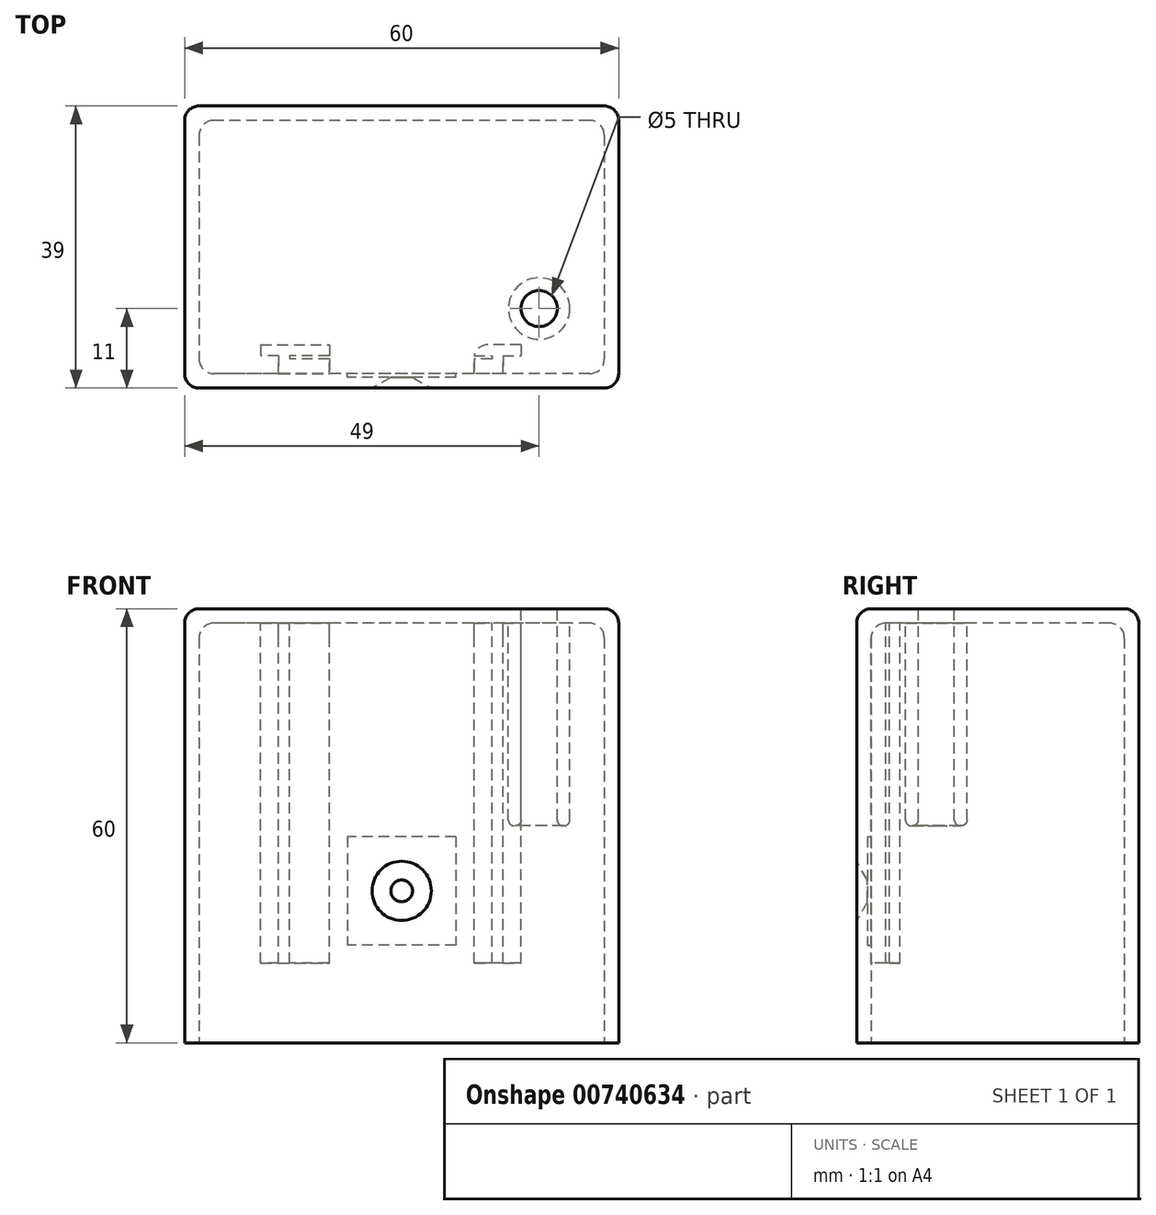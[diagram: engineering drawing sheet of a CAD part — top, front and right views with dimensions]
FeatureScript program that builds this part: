
annotation { "Feature Type Name" : "Feature", "Feature Type Description" : "" }
export const myFeature = defineFeature(function(context is Context, id is Id, definition is map)
    precondition{}
    {
        {
            var Q0;
            Q0=qCreatedBy(makeId("Top.planeOp"),FACE);
            var sketch = newSketch(context, id + "F0", { "sketchPlane" : qUnion([Q0])});
            skLineSegment(sketch, "E0.bottom", {"start": v(30, 19.5) * mm, "end": v(-30, 19.5) * mm});
            skLineSegment(sketch, "E0.top", {"start": v(30, -19.5) * mm, "end": v(-30, -19.5) * mm});
            skLineSegment(sketch, "E0.left", {"start": v(30, 19.5) * mm, "end": v(30, -19.5) * mm});
            skLineSegment(sketch, "E0.right", {"start": v(-30, 19.5) * mm, "end": v(-30, -19.5) * mm});
            skPoint(sketch, "E0.middle", {"position": v(0, 0) * mm});
            skSolve(sketch);
        }
        {
            var Q0;
            Q0 = qSketchRegion(id + "F0", true);
            extrude(context, id + "F1", {"entities" : qUnion([Q0]), "depth" : 60 * mm, "offsetDistance" : 25 * mm});
        }
        {
            var Q0;
            Q0=makeQuery(id+"F1.opExtrude","CAP_FACE",FACE,{"disambiguationData":[OSD([sQuery(id+"F0.wireOp",EDGE,"E0.bottom"),sQuery(id+"F0.wireOp",EDGE,"E0.top"),sQuery(id+"F0.wireOp",EDGE,"E0.left"),sQuery(id+"F0.wireOp",EDGE,"E0.right")])],"isStart":true});
            shell(context, id + "F2", {"entities" : qUnion([Q0]), "thickness" : 2 * mm});
        }
        {
            var Q0;
            Q0=makeQuery(id+"F1.opExtrude","SWEPT_EDGE",EDGE,{"disambiguationData":[OSD([sQuery(id+"F0.wireOp",EDGE,"E0.bottom"),sQuery(id+"F0.wireOp",EDGE,"E0.left")])]});
            var Q1;
            Q1=makeQuery(id+"F1.opExtrude","CAP_EDGE",EDGE,{"disambiguationData":[OSD([sQuery(id+"F0.wireOp",EDGE,"E0.bottom")])],"isStart":false});
            var Q2;
            Q2=makeQuery(id+"F1.opExtrude","SWEPT_EDGE",EDGE,{"disambiguationData":[OSD([sQuery(id+"F0.wireOp",EDGE,"E0.bottom"),sQuery(id+"F0.wireOp",EDGE,"E0.right")])]});
            var Q3;
            Q3=makeQuery(id+"F1.opExtrude","SWEPT_EDGE",EDGE,{"disambiguationData":[OSD([sQuery(id+"F0.wireOp",EDGE,"E0.top"),sQuery(id+"F0.wireOp",EDGE,"E0.right")])]});
            var Q4;
            Q4=makeQuery(id+"F1.opExtrude","CAP_EDGE",EDGE,{"disambiguationData":[OSD([sQuery(id+"F0.wireOp",EDGE,"E0.right")])],"isStart":false});
            var Q5;
            Q5=makeQuery(id+"F1.opExtrude","CAP_EDGE",EDGE,{"disambiguationData":[OSD([sQuery(id+"F0.wireOp",EDGE,"E0.top")])],"isStart":false});
            var Q6;
            Q6=makeQuery(id+"F1.opExtrude","SWEPT_EDGE",EDGE,{"disambiguationData":[OSD([sQuery(id+"F0.wireOp",EDGE,"E0.top"),sQuery(id+"F0.wireOp",EDGE,"E0.left")])]});
            var Q7;
            Q7=makeQuery(id+"F1.opExtrude","CAP_EDGE",EDGE,{"disambiguationData":[OSD([sQuery(id+"F0.wireOp",EDGE,"E0.left")])],"isStart":false});
            var Q8;
            Q8=makeQuery(id+"F2.opShell","OFFSET_EDGE",EDGE,{"disambiguationData":[OSD([sQuery(id+"F0.wireOp",EDGE,"E0.top"),sQuery(id+"F0.wireOp",EDGE,"E0.right")])]});
            var Q9;
            Q9=makeQuery(id+"F2.opShell","OFFSET_EDGE",EDGE,{"disambiguationData":[OSD([sQuery(id+"F0.wireOp",EDGE,"E0.top"),sQuery(id+"F0.wireOp",EDGE,"E0.left")])]});
            var Q10;
            {var subQ0=sQuery(id+"F0.wireOp",EDGE,"E0.bottom");var subQ1=sQuery(id+"F0.wireOp",EDGE,"E0.left");Q10=makeQuery(id+"F9EDMC7BK73mlxk_1.boolean.opBoolean","SPLIT",EDGE,{"disambiguationData":[topologyDisambiguationEdgeConnected([makeQuery(id+"F2.opShell","OFFSET_FACE",FACE,{"disambiguationData":[OSD([subQ0])]})])],"derivedFrom":makeQuery(id+"F2.opShell","OFFSET_EDGE",EDGE,{"disambiguationData":[OSD([subQ0,subQ1])]})});}
            var Q11;
            Q11=makeQuery(id+"F2.opShell","OFFSET_EDGE",EDGE,{"disambiguationData":[OSD([sQuery(id+"F0.wireOp",EDGE,"E0.bottom"),sQuery(id+"F0.wireOp",EDGE,"E0.right")])]});
            var Q12;
            {var subQ0=sQuery(id+"F0.wireOp",EDGE,"E0.bottom");Q12=makeQuery(id+"F2.opShell","OFFSET_EDGE",EDGE,{"disambiguationData":[OSD([subQ0]),TDD([makeQuery(id+"F1.opExtrude","CAP_EDGE",EDGE,{"disambiguationData":[OSD([subQ0])],"isStart":false})])]});}
            var Q13;
            {var subQ0=sQuery(id+"F0.wireOp",EDGE,"E0.right");Q13=makeQuery(id+"F2.opShell","OFFSET_EDGE",EDGE,{"disambiguationData":[OSD([subQ0]),TDD([makeQuery(id+"F1.opExtrude","CAP_EDGE",EDGE,{"disambiguationData":[OSD([subQ0])],"isStart":false})])]});}
            var Q14;
            {var subQ0=sQuery(id+"F0.wireOp",EDGE,"E0.left");Q14=makeQuery(id+"F2.opShell","OFFSET_EDGE",EDGE,{"disambiguationData":[OSD([subQ0]),TDD([makeQuery(id+"F1.opExtrude","CAP_EDGE",EDGE,{"disambiguationData":[OSD([subQ0])],"isStart":false})])]});}
            var Q15;
            {var subQ0=sQuery(id+"F0.wireOp",EDGE,"E0.top");Q15=makeQuery(id+"F2.opShell","OFFSET_EDGE",EDGE,{"disambiguationData":[OSD([subQ0]),TDD([makeQuery(id+"F1.opExtrude","CAP_EDGE",EDGE,{"disambiguationData":[OSD([subQ0])],"isStart":false})])]});}
            fillet(context, id + "F3", {"entities" : qUnion([Q0, Q1, Q2, Q3, Q4, Q5, Q6, Q7, Q8, Q9, Q10, Q11, Q12, Q13, Q14, Q15]), "radius" : 2 * mm, "tangentPropagation" : true, "allowEdgeOverflow" : false});
        }
        {
            var Q0;
            Q0=makeQuery(id+"F1.opExtrude","SWEPT_FACE",FACE,{"disambiguationData":[OSD([sQuery(id+"F0.wireOp",EDGE,"E0.top")])]});
            var sketch = newSketch(context, id + "F4", { "sketchPlane" : qUnion([Q0])});
            skLineSegment(sketch, "E1", {"start": v(-44.5, 21) * mm, "end": v(53.85, 21) * mm, "construction": true});
            skCircle(sketch, "E2", {"center": v(0, 21) * mm, "radius": 1.5 * mm});
            skSolve(sketch);
        }
        {
            var Q0;
            Q0 = qSketchRegion(id + "F4", true);
            extrude(context, id + "F5", {"entities" : qUnion([Q0]), "operationType" : NewBodyOperationType.REMOVE, "endBound" : BoundingType.SYMMETRIC, "oppositeDirection" : true, "depth" : 5 * mm, "offsetDistance" : 25 * mm});
        }
        {
            var Q0;
            Q0=makeQuery(id+"F2.opShell","OFFSET_FACE",FACE,{"disambiguationData":[OSD([sQuery(id+"F0.wireOp",EDGE,"E0.top")])]});
            var sketch = newSketch(context, id + "F6", { "sketchPlane" : qUnion([Q0])});
            skLineSegment(sketch, "E3.bottom", {"start": v(-7.5, 28.5) * mm, "end": v(7.5, 28.5) * mm});
            skLineSegment(sketch, "E3.top", {"start": v(-7.5, 13.5) * mm, "end": v(7.5, 13.5) * mm});
            skLineSegment(sketch, "E3.left", {"start": v(-7.5, 28.5) * mm, "end": v(-7.5, 13.5) * mm});
            skLineSegment(sketch, "E3.right", {"start": v(7.5, 28.5) * mm, "end": v(7.5, 13.5) * mm});
            skPoint(sketch, "E3.middle", {"position": v(0, 21) * mm});
            skSolve(sketch);
        }
        {
            var Q0;
            Q0=makeQuery(id+"F6.imprint","IMPRINT",FACE,{"disambiguationData":[TD([[makeQuery(id+"F6.imprint","IMPRINT",EDGE,{"derivedFrom":sQuery(id+"F6.wireOp",EDGE,"E3.bottom")}),-1.0]])]});
            extrude(context, id + "F7", {"entities" : qUnion([Q0]), "operationType" : NewBodyOperationType.REMOVE, "oppositeDirection" : true, "depth" : 0.5 * mm, "offsetDistance" : 25 * mm});
        }
        {
            var Q0;
            Q0=makeQuery(id+"F1.opExtrude","CAP_FACE",FACE,{"disambiguationData":[OSD([sQuery(id+"F0.wireOp",EDGE,"E0.bottom"),sQuery(id+"F0.wireOp",EDGE,"E0.top"),sQuery(id+"F0.wireOp",EDGE,"E0.left"),sQuery(id+"F0.wireOp",EDGE,"E0.right")])],"isStart":false});
            var sketch = newSketch(context, id + "F8", { "sketchPlane" : qUnion([Q0])});
            skCircle(sketch, "E4", {"center": v(19, -8.5) * mm, "radius": 4.25 * mm});
            skCircle(sketch, "E5", {"center": v(19, -8.5) * mm, "radius": 2.5 * mm});
            skSolve(sketch);
        }
        {
            var Q0;
            Q0=makeQuery(id+"F8.imprint","IMPRINT",FACE,{"disambiguationData":[TD([[makeQuery(id+"F8.imprint","IMPRINT",EDGE,{"derivedFrom":sQuery(id+"F8.wireOp",EDGE,"E4")}),1.0]])]});
            extrude(context, id + "F9", {"entities" : qUnion([Q0]), "operationType" : NewBodyOperationType.ADD, "oppositeDirection" : true, "depth" : 30 * mm, "offsetDistance" : 25 * mm});
        }
        {
            var Q0;
            Q0=makeQuery(id+"F8.imprint","IMPRINT",FACE,{"disambiguationData":[TD([[makeQuery(id+"F8.imprint","IMPRINT",EDGE,{"derivedFrom":sQuery(id+"F8.wireOp",EDGE,"E5")}),1.0]])]});
            extrude(context, id + "F10", {"entities" : qUnion([Q0]), "operationType" : NewBodyOperationType.REMOVE, "endBound" : BoundingType.SYMMETRIC, "oppositeDirection" : true, "depth" : 90 * mm, "offsetDistance" : 25 * mm});
        }
        {
            var Q0;
            {var subQ0=sQuery(id+"F0.wireOp",EDGE,"E0.right");var subQ1=sQuery(id+"F0.wireOp",EDGE,"E0.top");var subQ2=sQuery(id+"F0.wireOp",EDGE,"E0.left");var subQ3=sQuery(id+"F0.wireOp",EDGE,"E0.bottom");Q0=makeQuery(id+"F9.boolean.opBoolean","SPLIT",FACE,{"disambiguationData":[TD([makeQuery(id+"F9.opExtrude","SWEPT_FACE",FACE,{"disambiguationData":[OSD([sQuery(id+"F8.wireOp",EDGE,"E4")])]})])],"derivedFrom":makeQuery(id+"F2.opShell","OFFSET_FACE",FACE,{"disambiguationData":[OSD([subQ3,subQ1,subQ2,subQ0])]})});}
            var sketch = newSketch(context, id + "F11", { "sketchPlane" : qUnion([Q0])});
            skLineSegment(sketch, "E6.0", {"start": v(26, 17.5) * mm, "end": v(-26, 17.5) * mm, "construction": true});
            skLineSegment(sketch, "E7.bottom", {"start": v(-17, 17.5) * mm, "end": v(-10, 17.5) * mm});
            skLineSegment(sketch, "E7.top", {"start": v(-17, 13.5) * mm, "end": v(-10, 13.5) * mm});
            skLineSegment(sketch, "E7.left", {"start": v(-17, 13.5) * mm, "end": v(-17, 17.5) * mm});
            skLineSegment(sketch, "E7.right", {"start": v(-10, 13.5) * mm, "end": v(-10, 17.5) * mm});
            skLineSegment(sketch, "E8.bottom", {"start": v(14, 17.5) * mm, "end": v(10, 17.5) * mm});
            skLineSegment(sketch, "E8.top", {"start": v(14, 13.5) * mm, "end": v(10, 13.5) * mm});
            skLineSegment(sketch, "E8.left", {"start": v(14, 13.5) * mm, "end": v(14, 17.5) * mm});
            skLineSegment(sketch, "E8.right", {"start": v(10, 13.5) * mm, "end": v(10, 17.5) * mm});
            skLineSegment(sketch, "E9.bottom", {"start": v(-10, 17.5) * mm, "end": v(-15.5, 17.5) * mm});
            skLineSegment(sketch, "E9.top", {"start": v(-10, 15) * mm, "end": v(-15.5, 15) * mm});
            skLineSegment(sketch, "E9.left", {"start": v(-10, 15) * mm, "end": v(-10, 17.5) * mm});
            skLineSegment(sketch, "E9.right", {"start": v(-15.5, 15) * mm, "end": v(-15.5, 17.5) * mm});
            skLineSegment(sketch, "E10.bottom", {"start": v(10, 17.5) * mm, "end": v(12.5, 17.5) * mm});
            skLineSegment(sketch, "E10.top", {"start": v(10, 15) * mm, "end": v(12.5, 15) * mm});
            skLineSegment(sketch, "E10.left", {"start": v(10, 15) * mm, "end": v(10, 17.5) * mm});
            skLineSegment(sketch, "E10.right", {"start": v(12.5, 15) * mm, "end": v(12.5, 17.5) * mm});
            skLineSegment(sketch, "E11.bottom", {"start": v(-17, 13.5) * mm, "end": v(-19.5, 13.5) * mm});
            skLineSegment(sketch, "E11.top", {"start": v(-17, 15) * mm, "end": v(-19.5, 15) * mm});
            skLineSegment(sketch, "E11.left", {"start": v(-17, 13.5) * mm, "end": v(-17, 15) * mm});
            skLineSegment(sketch, "E11.right", {"start": v(-19.5, 13.5) * mm, "end": v(-19.5, 15) * mm});
            skLineSegment(sketch, "E12.bottom", {"start": v(14, 13.5) * mm, "end": v(16.5, 13.5) * mm});
            skLineSegment(sketch, "E12.top", {"start": v(14, 15) * mm, "end": v(16.5, 15) * mm});
            skLineSegment(sketch, "E12.left", {"start": v(14, 13.5) * mm, "end": v(14, 15) * mm});
            skLineSegment(sketch, "E12.right", {"start": v(16.5, 13.5) * mm, "end": v(16.5, 15) * mm});
            skSolve(sketch);
        }
        {
            var Q0;
            {var subQ1=sQuery(id+"F11.wireOp",EDGE,"E7.top");Q0=makeQuery(id+"F11.imprint","IMPRINT",FACE,{"disambiguationData":[TD([[makeQuery(id+"F11.imprint","IMPRINT",EDGE,{"derivedFrom":subQ1}),1.0]])]});}
            var Q1;
            {var subQ0=sQuery(id+"F11.wireOp",EDGE,"E7.bottom");Q1=makeQuery(id+"F11.imprint","IMPRINT",FACE,{"disambiguationData":[TD([[makeQuery(id+"F11.imprint","IMPRINT",EDGE,{"derivedFrom":subQ0}),-1.0]])]});}
            var Q2;
            {var subQ0=sQuery(id+"F11.wireOp",EDGE,"E8.bottom");Q2=makeQuery(id+"F11.imprint","IMPRINT",FACE,{"disambiguationData":[TD([[makeQuery(id+"F11.imprint","IMPRINT",EDGE,{"derivedFrom":subQ0}),1.0]])]});}
            var Q3;
            {var subQ5=sQuery(id+"F11.wireOp",EDGE,"E8.top");Q3=makeQuery(id+"F11.imprint","IMPRINT",FACE,{"disambiguationData":[TD([[makeQuery(id+"F11.imprint","IMPRINT",EDGE,{"derivedFrom":subQ5}),-1.0]])]});}
            var Q4;
            Q4=makeQuery(id+"F11.imprint","IMPRINT",FACE,{"disambiguationData":[TD([[makeQuery(id+"F11.imprint","IMPRINT",EDGE,{"derivedFrom":sQuery(id+"F11.wireOp",EDGE,"E11.bottom")}),-1.0]])]});
            var Q5;
            Q5=makeQuery(id+"F11.imprint","IMPRINT",FACE,{"disambiguationData":[TD([[makeQuery(id+"F11.imprint","IMPRINT",EDGE,{"derivedFrom":sQuery(id+"F11.wireOp",EDGE,"E12.bottom")}),1.0]])]});
            var Q6;
            {var subQ0=sQuery(id+"F0.wireOp",EDGE,"E0.right");var subQ1=sQuery(id+"F0.wireOp",EDGE,"E0.top");var subQ2=sQuery(id+"F0.wireOp",EDGE,"E0.left");var subQ3=sQuery(id+"F0.wireOp",EDGE,"E0.bottom");Q6=makeQuery(id+"F9.boolean.opBoolean","SPLIT",FACE,{"disambiguationData":[TD([makeQuery(id+"F9.opExtrude","SWEPT_FACE",FACE,{"disambiguationData":[OSD([sQuery(id+"F8.wireOp",EDGE,"E4")])]})])],"derivedFrom":makeQuery(id+"F2.opShell","OFFSET_FACE",FACE,{"disambiguationData":[OSD([subQ3,subQ1,subQ2,subQ0])]})});}
            extrude(context, id + "F12", {"entities" : qUnion([Q0, Q1, Q2, Q3, Q4, Q5]), "operationType" : NewBodyOperationType.ADD, "depth" : 47 * mm, "endBoundEntityFace" : qUnion([Q6]), "offsetDistance" : 25 * mm});
        }
        {
            var Q0;
            Q0=makeQuery(id+"F9.opExtrude","CAP_EDGE",EDGE,{"disambiguationData":[OSD([sQuery(id+"F8.wireOp",EDGE,"E4")])],"isStart":false});
            var Q1;
            Q1=makeQuery(id+"F9.opExtrude","CAP_EDGE",EDGE,{"disambiguationData":[OSD([sQuery(id+"F8.wireOp",EDGE,"E5")])],"isStart":false});
            fillet(context, id + "F13", {"entities" : qUnion([Q0, Q1]), "radius" : 0.8 * mm, "tangentPropagation" : true, "allowEdgeOverflow" : false});
        }
        {
            var Q0;
            Q0=makeQuery(id+"F5.boolean.opBoolean","INTERSECT",EDGE,{"derivedFrom":[makeQuery(id+"F1.opExtrude","SWEPT_FACE",FACE,{"disambiguationData":[OSD([sQuery(id+"F0.wireOp",EDGE,"E0.top")])]}),makeQuery(id+"F5.opExtrude","SWEPT_FACE",FACE,{"disambiguationData":[OSD([sQuery(id+"F4.wireOp",EDGE,"E2")])]})]});
            chamfer(context, id + "F14", {"entities" : qUnion([Q0]), "chamferType" : ChamferType.OFFSET_ANGLE, "width" : 1.5 * mm, "oppositeDirection" : false, "angle" : 60 * degree, "tangentPropagation" : true});
        }
        {
            var Q0;
            Q0=makeQuery(id+"F12.opExtrude","SWEPT_EDGE",EDGE,{"disambiguationData":[OSD([sQuery(id+"F11.wireOp",EDGE,"E8.top"),sQuery(id+"F11.wireOp",EDGE,"E8.right")])]});
            var Q1;
            Q1=makeQuery(id+"F12.opExtrude","CAP_EDGE",EDGE,{"disambiguationData":[OSD([sQuery(id+"F11.wireOp",EDGE,"E7.top"),sQuery(id+"F11.wireOp",EDGE,"E11.bottom")])],"isStart":true});
            var Q2;
            Q2=makeQuery(id+"F12.opExtrude","CAP_EDGE",EDGE,{"disambiguationData":[OSD([sQuery(id+"F11.wireOp",EDGE,"E8.top"),sQuery(id+"F11.wireOp",EDGE,"E12.bottom")])],"isStart":true});
            var Q3;
            Q3=makeQuery(id+"F12.opExtrude","CAP_EDGE",EDGE,{"disambiguationData":[OSD([sQuery(id+"F11.wireOp",EDGE,"E12.right")])],"isStart":true});
            var Q4;
            Q4=makeQuery(id+"F12.opExtrude","CAP_EDGE",EDGE,{"disambiguationData":[OSD([sQuery(id+"F11.wireOp",EDGE,"E12.top")])],"isStart":true});
            var Q5;
            Q5=makeQuery(id+"F12.opExtrude","CAP_EDGE",EDGE,{"disambiguationData":[OSD([sQuery(id+"F11.wireOp",EDGE,"E11.right")])],"isStart":true});
            var Q6;
            Q6=makeQuery(id+"F12.opExtrude","CAP_EDGE",EDGE,{"disambiguationData":[OSD([sQuery(id+"F11.wireOp",EDGE,"E11.top")])],"isStart":true});
            fillet(context, id + "F15", {"entities" : qUnion([Q0, Q1, Q2, Q3, Q4, Q5, Q6]), "radius" : 2 * mm, "tangentPropagation" : true, "allowEdgeOverflow" : false});
        }
    });
